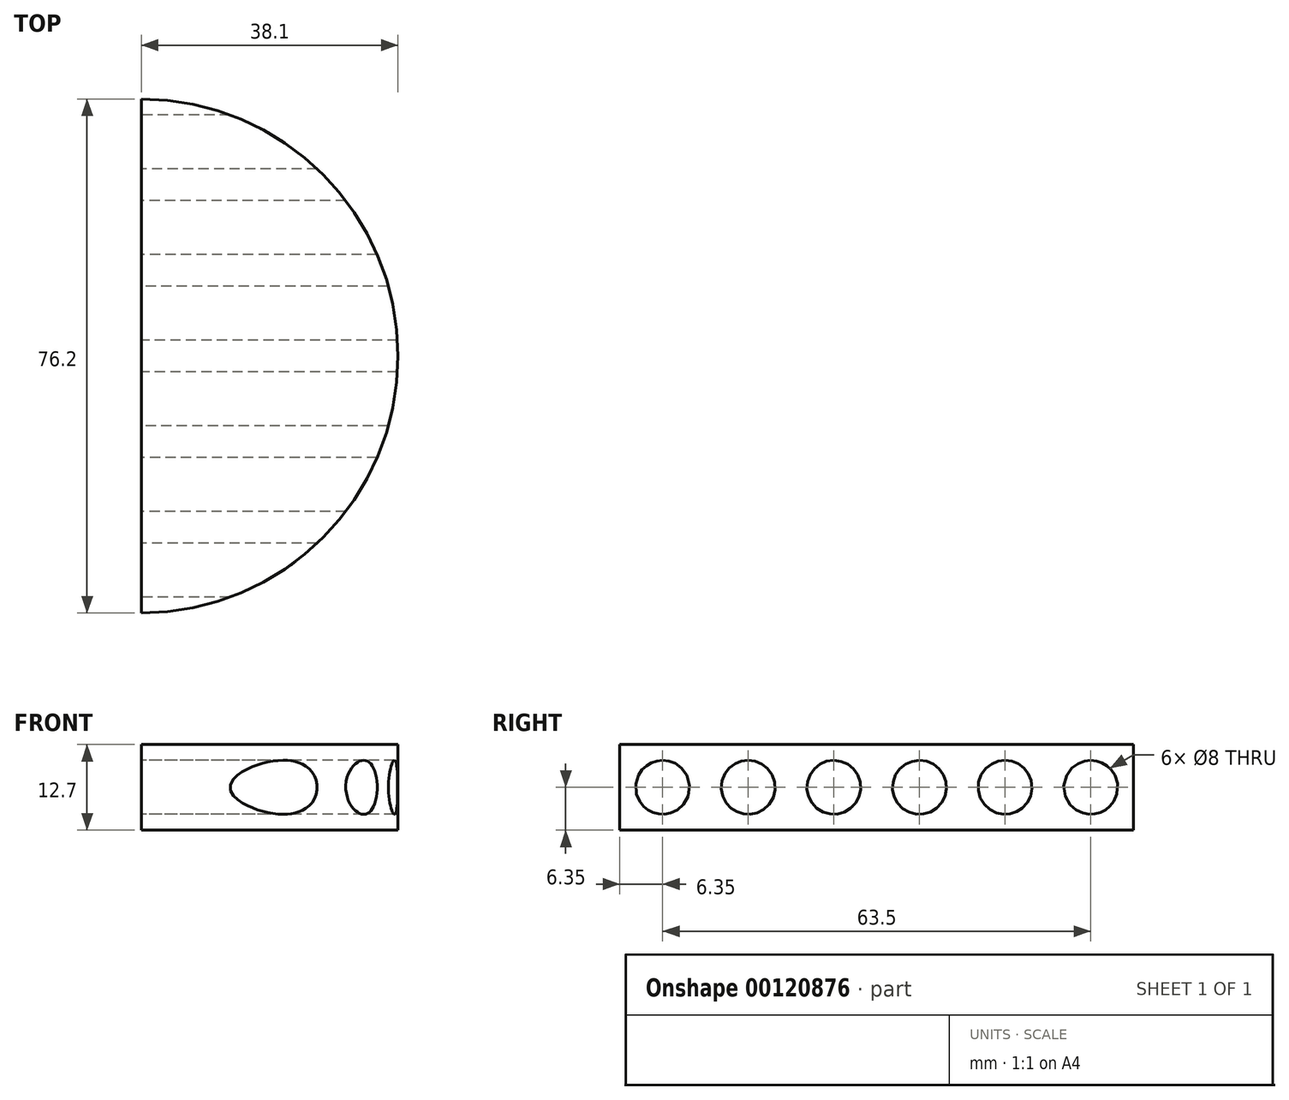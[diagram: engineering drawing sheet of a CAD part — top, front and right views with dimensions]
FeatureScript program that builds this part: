
annotation { "Feature Type Name" : "Feature", "Feature Type Description" : "" }
export const myFeature = defineFeature(function(context is Context, id is Id, definition is map)
    precondition{}
    {
        {
            var Q0;
            Q0=qCreatedBy(makeId("Top.planeOp"),FACE);
            var sketch = newSketch(context, id + "F0", { "sketchPlane" : qUnion([Q0])});
            skCircle(sketch, "E0", {"center": v(0, 0) * mm, "radius": 38.1 * mm});
            skSolve(sketch);
        }
        {
            var Q0;
            Q0=qSketchRegion(id+"F0",true);
            extrude(context, id + "F1", {"entities" : qUnion([Q0]), "depth" : 12.7 * mm});
        }
        {
            var Q0;
            Q0=makeQuery(id+"F1.opExtrude","CAP_FACE",FACE,{"disambiguationData":[OSD([sQuery(id+"F0.wireOp",EDGE,"E0")])],"isStart":false});
            var sketch = newSketch(context, id + "F2", { "sketchPlane" : qUnion([Q0])});
            skLineSegment(sketch, "E1.bottom", {"start": v(0, 47.06) * mm, "end": v(-42.45, 47.06) * mm});
            skLineSegment(sketch, "E1.top", {"start": v(0, -44.26) * mm, "end": v(-42.45, -44.26) * mm});
            skLineSegment(sketch, "E1.left", {"start": v(0, 47.06) * mm, "end": v(0, -44.26) * mm});
            skLineSegment(sketch, "E1.right", {"start": v(-42.45, 47.06) * mm, "end": v(-42.45, -44.26) * mm});
            skSolve(sketch);
        }
        {
            var Q0;
            Q0 = qSketchRegion(id + "F2", true);
            extrude(context, id + "F3", {"entities" : qUnion([Q0]), "operationType" : NewBodyOperationType.REMOVE, "endBound" : BoundingType.UP_TO_NEXT, "oppositeDirection" : true, "depth" : 25.4 * mm});
        }
        {
            var Q0;
            Q0=makeQuery(id+"F3.boolean.opBoolean","COPY",FACE,{"derivedFrom":makeQuery(id+"F3.opExtrude","SWEPT_FACE",FACE,{"disambiguationData":[OSD([sQuery(id+"F2.wireOp",EDGE,"E1.left")])]})});
            var sketch = newSketch(context, id + "F4", { "sketchPlane" : qUnion([Q0])});
            skCircle(sketch, "E2", {"center": v(-31.75, 6.35) * mm, "radius": 4 * mm});
            skCircle(sketch, "E3.1.0.0", {"center": v(-19.05, 6.35) * mm, "radius": 4 * mm});
            skCircle(sketch, "E3.2.0.0", {"center": v(-6.35, 6.35) * mm, "radius": 4 * mm});
            skCircle(sketch, "E3.3.0.0", {"center": v(6.35, 6.35) * mm, "radius": 4 * mm});
            skCircle(sketch, "E3.4.0.0", {"center": v(19.05, 6.35) * mm, "radius": 4 * mm});
            skCircle(sketch, "E3.5.0.0", {"center": v(31.75, 6.35) * mm, "radius": 4 * mm});
            skLineSegment(sketch, "E3.direction1", {"start": v(-31.75, 6.35) * mm, "end": v(-19.05, 6.35) * mm, "construction": true});
            skSolve(sketch);
        }
        {
            var Q0;
            Q0 = qSketchRegion(id + "F4", true);
            extrude(context, id + "F5", {"entities" : qUnion([Q0]), "operationType" : NewBodyOperationType.REMOVE, "endBound" : BoundingType.THROUGH_ALL, "oppositeDirection" : true, "depth" : 25 * mm});
        }
    });
